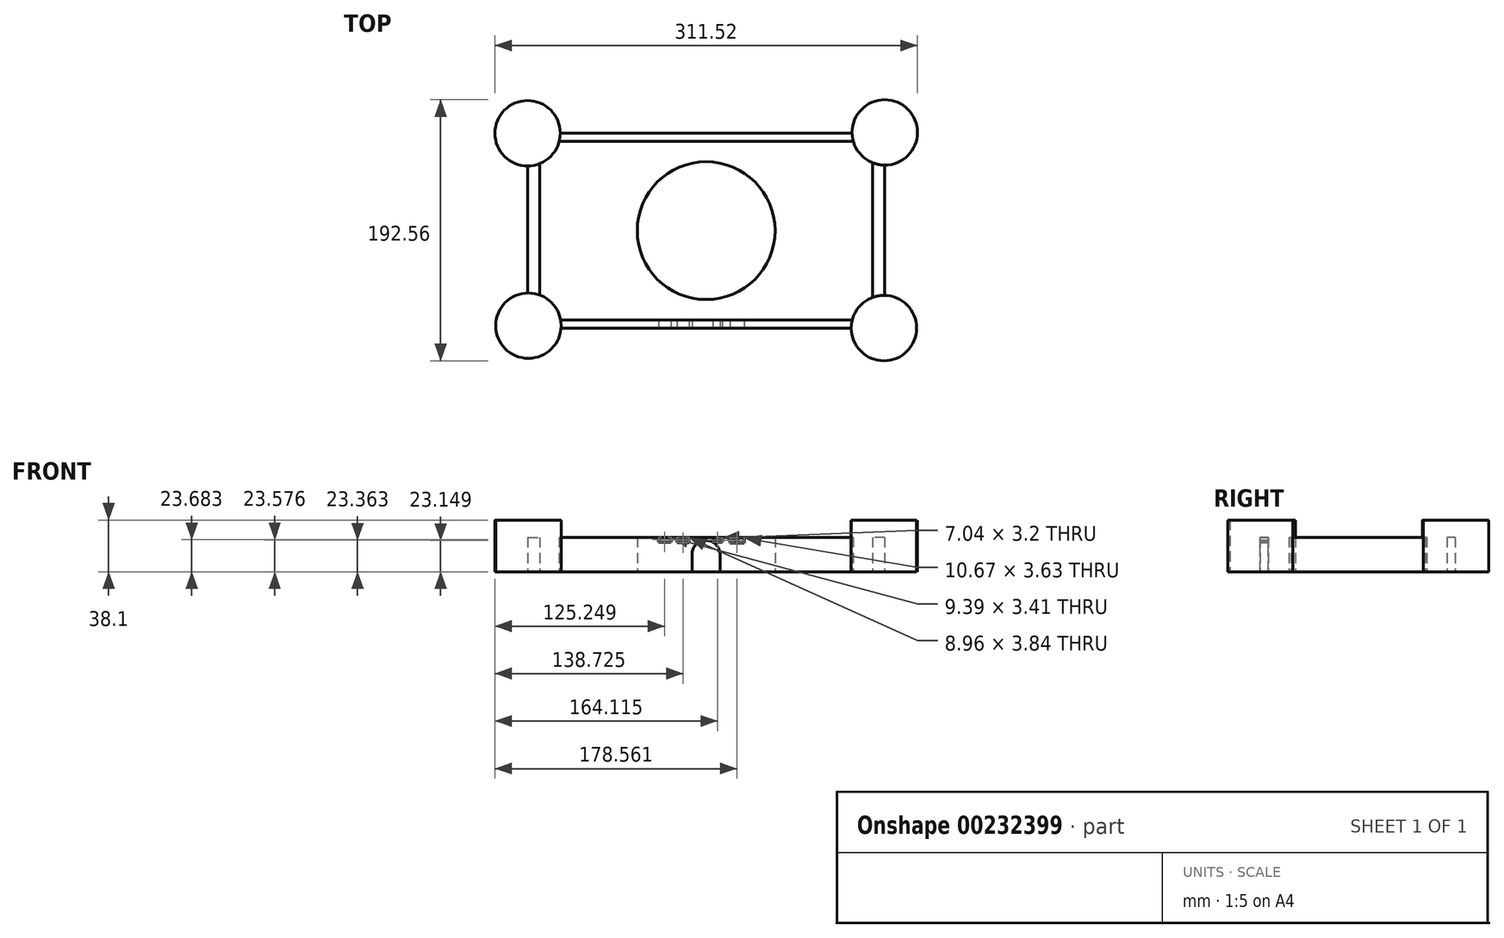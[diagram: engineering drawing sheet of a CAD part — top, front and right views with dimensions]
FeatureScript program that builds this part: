
annotation { "Feature Type Name" : "Feature", "Feature Type Description" : "" }
export const myFeature = defineFeature(function(context is Context, id is Id, definition is map)
    precondition{}
    {
        {
            var Q0;
            Q0=qCreatedBy(makeId("Top.planeOp"),FACE);
            var sketch = newSketch(context, id + "F0", { "sketchPlane" : qUnion([Q0])});
            skLineSegment(sketch, "E0.bottom", {"start": v(131.65, -71.86) * mm, "end": v(131.05, -71.86) * mm});
            skLineSegment(sketch, "E0.top", {"start": v(107.55, 71.86) * mm, "end": v(-107.54, 71.86) * mm});
            skLineSegment(sketch, "E0.left", {"start": v(131.65, -47.76) * mm, "end": v(131.65, 48.36) * mm});
            skLineSegment(sketch, "E0.right", {"start": v(-131.65, -45.95) * mm, "end": v(-131.65, 47.75) * mm});
            skPoint(sketch, "E0.middle", {"position": v(0, 0) * mm});
            skCircle(sketch, "E1", {"center": v(0, 0) * mm, "radius": 50.8 * mm});
            skCircle(sketch, "E2", {"center": v(-131.65, 71.86) * mm, "radius": 24.11 * mm});
            skCircle(sketch, "E3", {"center": v(131.65, 72.47) * mm, "radius": 24.11 * mm});
            skCircle(sketch, "E4", {"center": v(131.05, -71.86) * mm, "radius": 24.11 * mm});
            skCircle(sketch, "E5", {"center": v(-131.07, -70.05) * mm, "radius": 24.11 * mm});
            skLineSegment(sketch, "E6.bottom", {"start": v(108.47, 65.83) * mm, "end": v(-108.3, 65.83) * mm});
            skLineSegment(sketch, "E6.top", {"start": v(107.7, -65.83) * mm, "end": v(-107.33, -65.83) * mm});
            skLineSegment(sketch, "E6.left", {"start": v(122.6, 50.12) * mm, "end": v(122.6, -49.29) * mm});
            skLineSegment(sketch, "E6.right", {"start": v(-122.6, 49.52) * mm, "end": v(-122.6, -47.48) * mm});
            skPoint(sketch, "E7.orphan", {"position": v(131.65, 71.86) * mm});
            skLineSegment(sketch, "E8.trimOffspring", {"start": v(106.94, -71.86) * mm, "end": v(-107.03, -71.86) * mm});
            skPoint(sketch, "E9.orphan", {"position": v(122.6, -65.83) * mm});
            skPoint(sketch, "E10.orphan", {"position": v(-122.6, -65.83) * mm});
            skPoint(sketch, "E11.orphan", {"position": v(-131.65, -71.86) * mm});
            skPoint(sketch, "E12.orphan", {"position": v(-122.6, 65.83) * mm});
            skPoint(sketch, "E13.orphan", {"position": v(122.6, 65.83) * mm});
            skSolve(sketch);
        }
        {
            var Q0;
            {var subQ0=sQuery(id+"F0.wireOp",EDGE,"E0.top");Q0=makeQuery(id+"F0.imprint","IMPRINT",FACE,{"disambiguationData":[TD([[makeQuery(id+"F0.imprint","IMPRINT",EDGE,{"derivedFrom":subQ0}),1.0]])]});}
            var Q1;
            {var subQ0=sQuery(id+"F0.wireOp",EDGE,"E0.right");Q1=makeQuery(id+"F0.imprint","IMPRINT",FACE,{"disambiguationData":[TD([[makeQuery(id+"F0.imprint","IMPRINT",EDGE,{"derivedFrom":subQ0}),-1.0]])]});}
            var Q2;
            {var subQ0=sQuery(id+"F0.wireOp",EDGE,"E6.top");Q2=makeQuery(id+"F0.imprint","IMPRINT",FACE,{"disambiguationData":[TD([[makeQuery(id+"F0.imprint","IMPRINT",EDGE,{"derivedFrom":subQ0}),1.0]])]});}
            var Q3;
            {var subQ0=sQuery(id+"F0.wireOp",EDGE,"E0.left");Q3=makeQuery(id+"F0.imprint","IMPRINT",FACE,{"disambiguationData":[TD([[makeQuery(id+"F0.imprint","IMPRINT",EDGE,{"derivedFrom":subQ0}),1.0]])]});}
            extrude(context, id + "F1", {"entities" : qUnion([Q0, Q1, Q2, Q3]), "depth" : 25.4 * mm});
        }
        {
            var Q0;
            {var subQ0=sQuery(id+"F0.wireOp",EDGE,"E2");var subQ1=makeQuery(id+"F0.imprint","INTERSECT",VERTEX,{"derivedFrom":[sQuery(id+"F0.wireOp",EDGE,"E0.top"),subQ0]});Q0=makeQuery(id+"F0.imprint","IMPRINT",FACE,{"disambiguationData":[TD([[makeQuery(id+"F0.imprint","IMPRINT",EDGE,{"disambiguationData":[TD([[subQ1,-1.0]])],"derivedFrom":subQ0}),1.0]])]});}
            var Q1;
            {var subQ0=sQuery(id+"F0.wireOp",EDGE,"E3");var subQ1=makeQuery(id+"F0.imprint","INTERSECT",VERTEX,{"derivedFrom":[sQuery(id+"F0.wireOp",EDGE,"E0.top"),subQ0]});Q1=makeQuery(id+"F0.imprint","IMPRINT",FACE,{"disambiguationData":[TD([[makeQuery(id+"F0.imprint","IMPRINT",EDGE,{"disambiguationData":[TD([[subQ1,-1.0]])],"derivedFrom":subQ0}),1.0]])]});}
            var Q2;
            {var subQ0=sQuery(id+"F0.wireOp",EDGE,"E5");var subQ1=makeQuery(id+"F0.imprint","INTERSECT",VERTEX,{"derivedFrom":[subQ0,sQuery(id+"F0.wireOp",EDGE,"E6.top")]});Q2=makeQuery(id+"F0.imprint","IMPRINT",FACE,{"disambiguationData":[TD([[makeQuery(id+"F0.imprint","IMPRINT",EDGE,{"disambiguationData":[TD([[subQ1,-1.0]])],"derivedFrom":subQ0}),1.0]])]});}
            var Q3;
            {var subQ0=sQuery(id+"F0.wireOp",EDGE,"E4");var subQ1=makeQuery(id+"F0.imprint","INTERSECT",VERTEX,{"derivedFrom":[sQuery(id+"F0.wireOp",EDGE,"E0.left"),subQ0]});Q3=makeQuery(id+"F0.imprint","IMPRINT",FACE,{"disambiguationData":[TD([[makeQuery(id+"F0.imprint","IMPRINT",EDGE,{"disambiguationData":[TD([[subQ1,-1.0]])],"derivedFrom":subQ0}),1.0]])]});}
            extrude(context, id + "F2", {"entities" : qUnion([Q0, Q1, Q2, Q3]), "depth" : 38.1 * mm});
        }
        {
            var Q0;
            Q0=makeQuery(id+"F1.opExtrude","SWEPT_FACE",FACE,{"disambiguationData":[OSD([sQuery(id+"F0.wireOp",EDGE,"E8.trimOffspring")])]});
            var sketch = newSketch(context, id + "F3", { "sketchPlane" : qUnion([Q0])});
            skLineSegment(sketch, "E14.bottom", {"start": v(-10.48, 0) * mm, "end": v(10.21, 0) * mm});
            skLineSegment(sketch, "E14.left", {"start": v(-10.48, 0) * mm, "end": v(-10.48, 12.8) * mm});
            skLineSegment(sketch, "E14.right", {"start": v(10.21, 0) * mm, "end": v(10.21, 12.8) * mm});
            skArc(sketch, "E15", {"start": v(10.21, 12.8) * mm, "mid": v(-0.14, 23.15) * mm, "end": v(-10.48, 12.8) * mm});
            skLineSegment(sketch, "E16.bottom", {"start": v(-26.67, 20.7) * mm, "end": v(-34.35, 20.7) * mm});
            skLineSegment(sketch, "E16.top", {"start": v(-26.67, 25.39) * mm, "end": v(-34.35, 25.39) * mm});
            skLineSegment(sketch, "E16.left", {"start": v(-26.67, 20.7) * mm, "end": v(-26.67, 25.39) * mm});
            skLineSegment(sketch, "E16.right", {"start": v(-34.35, 20.7) * mm, "end": v(-34.35, 25.39) * mm});
            skPoint(sketch, "E16.middle", {"position": v(-30.51, 23.04) * mm});
            skLineSegment(sketch, "E17.bottom", {"start": v(-15.65, 20.95) * mm, "end": v(-23.65, 20.95) * mm});
            skLineSegment(sketch, "E17.top", {"start": v(-15.65, 25.18) * mm, "end": v(-23.65, 25.18) * mm});
            skLineSegment(sketch, "E17.left", {"start": v(-15.65, 20.95) * mm, "end": v(-15.65, 25.18) * mm});
            skLineSegment(sketch, "E17.right", {"start": v(-23.65, 20.95) * mm, "end": v(-23.65, 25.18) * mm});
            skPoint(sketch, "E17.middle", {"position": v(-19.65, 23.06) * mm});
            skLineSegment(sketch, "E18.bottom", {"start": v(-6.52, 22.23) * mm, "end": v(-12.1, 22.23) * mm});
            skLineSegment(sketch, "E18.top", {"start": v(-6.52, 25.25) * mm, "end": v(-12.1, 25.25) * mm});
            skLineSegment(sketch, "E18.left", {"start": v(-6.52, 22.23) * mm, "end": v(-6.52, 25.25) * mm});
            skLineSegment(sketch, "E18.right", {"start": v(-12.1, 22.23) * mm, "end": v(-12.1, 25.25) * mm});
            skPoint(sketch, "E18.middle", {"position": v(-9.31, 23.74) * mm});
            skLineSegment(sketch, "E19.bottom", {"start": v(3.56, 23.15) * mm, "end": v(-3.65, 23.15) * mm});
            skLineSegment(sketch, "E19.top", {"start": v(3.56, 25.64) * mm, "end": v(-3.65, 25.64) * mm});
            skLineSegment(sketch, "E19.left", {"start": v(3.56, 23.15) * mm, "end": v(3.56, 25.64) * mm});
            skLineSegment(sketch, "E19.right", {"start": v(-3.65, 23.15) * mm, "end": v(-3.65, 25.64) * mm});
            skPoint(sketch, "E19.middle", {"position": v(-0.04, 24.4) * mm});
            skPoint(sketch, "E19.middle.positionSnap0", {"position": v(-0.04, 25.4) * mm});
            skPoint(sketch, "E19.cornerSnap0", {"position": v(-0.14, 23.15) * mm});
            skPoint(sketch, "E19.centerSnap0", {"position": v(-0.04, 25.4) * mm});
            skLineSegment(sketch, "E20.bottom", {"start": v(16.8, 20.98) * mm, "end": v(6.55, 20.98) * mm});
            skLineSegment(sketch, "E20.top", {"start": v(16.8, 25.32) * mm, "end": v(6.55, 25.32) * mm});
            skLineSegment(sketch, "E20.left", {"start": v(16.8, 20.98) * mm, "end": v(16.8, 25.32) * mm});
            skLineSegment(sketch, "E20.right", {"start": v(6.55, 20.98) * mm, "end": v(6.55, 25.32) * mm});
            skPoint(sketch, "E20.middle", {"position": v(11.67, 23.15) * mm});
            skLineSegment(sketch, "E21.bottom", {"start": v(30.23, 21.3) * mm, "end": v(19.56, 21.3) * mm});
            skLineSegment(sketch, "E21.top", {"start": v(30.23, 25) * mm, "end": v(19.56, 25) * mm});
            skLineSegment(sketch, "E21.left", {"start": v(30.23, 21.3) * mm, "end": v(30.23, 25) * mm});
            skLineSegment(sketch, "E21.right", {"start": v(19.56, 21.3) * mm, "end": v(19.56, 25) * mm});
            skPoint(sketch, "E21.middle", {"position": v(24.9, 23.15) * mm});
            skSolve(sketch);
        }
        {
            var Q0;
            Q0=makeQuery(id+"F3.imprint","IMPRINT",FACE,{"disambiguationData":[TD([[makeQuery(id+"F3.imprint","IMPRINT",EDGE,{"derivedFrom":sQuery(id+"F3.wireOp",EDGE,"E14.bottom")}),-1.0]])]});
            extrude(context, id + "F4", {"entities" : qUnion([Q0]), "operationType" : NewBodyOperationType.REMOVE, "oppositeDirection" : true, "depth" : 25.4 * mm});
        }
        {
            var Q0;
            Q0=makeQuery(id+"F1.opExtrude","SWEPT_FACE",FACE,{"disambiguationData":[OSD([sQuery(id+"F0.wireOp",EDGE,"E8.trimOffspring")])]});
            var sketch = newSketch(context, id + "F5", { "sketchPlane" : qUnion([Q0])});
            skLineSegment(sketch, "E22.bottom", {"start": v(-25.82, 21.98) * mm, "end": v(-35.2, 21.98) * mm});
            skLineSegment(sketch, "E22.top", {"start": v(-25.82, 25.39) * mm, "end": v(-35.2, 25.39) * mm});
            skLineSegment(sketch, "E22.left", {"start": v(-25.82, 21.98) * mm, "end": v(-25.82, 25.39) * mm});
            skLineSegment(sketch, "E22.right", {"start": v(-35.2, 21.98) * mm, "end": v(-35.2, 25.39) * mm});
            skPoint(sketch, "E22.middle", {"position": v(-30.51, 23.68) * mm});
            skLineSegment(sketch, "E23.bottom", {"start": v(28.13, 21.34) * mm, "end": v(17.47, 21.34) * mm});
            skLineSegment(sketch, "E23.top", {"start": v(28.13, 24.96) * mm, "end": v(17.47, 24.96) * mm});
            skLineSegment(sketch, "E23.left", {"start": v(28.13, 21.34) * mm, "end": v(28.13, 24.96) * mm});
            skLineSegment(sketch, "E23.right", {"start": v(17.47, 21.34) * mm, "end": v(17.47, 24.96) * mm});
            skPoint(sketch, "E23.middle", {"position": v(22.8, 23.15) * mm});
            skPoint(sketch, "E23.middle.positionSnap0", {"position": v(-0.14, 23.15) * mm});
            skPoint(sketch, "E23.centerSnap0", {"position": v(-0.14, 23.15) * mm});
            skSolve(sketch);
        }
        {
            var Q0;
            Q0=makeQuery(id+"F5.imprint","IMPRINT",FACE,{"disambiguationData":[TD([[makeQuery(id+"F5.imprint","IMPRINT",EDGE,{"derivedFrom":sQuery(id+"F5.wireOp",EDGE,"E22.bottom")}),-1.0]])]});
            var Q1;
            Q1=makeQuery(id+"F5.imprint","IMPRINT",FACE,{"disambiguationData":[TD([[makeQuery(id+"F5.imprint","IMPRINT",EDGE,{"derivedFrom":sQuery(id+"F5.wireOp",EDGE,"E23.bottom")}),-1.0]])]});
            extrude(context, id + "F6", {"entities" : qUnion([Q0, Q1]), "operationType" : NewBodyOperationType.REMOVE, "oppositeDirection" : true, "depth" : 25.4 * mm});
        }
        {
            var Q0;
            Q0=makeQuery(id+"F1.opExtrude","SWEPT_FACE",FACE,{"disambiguationData":[OSD([sQuery(id+"F0.wireOp",EDGE,"E8.trimOffspring")])]});
            var sketch = newSketch(context, id + "F7", { "sketchPlane" : qUnion([Q0])});
            skLineSegment(sketch, "E24.bottom", {"start": v(-12.55, 21.44) * mm, "end": v(-21.52, 21.44) * mm});
            skLineSegment(sketch, "E24.top", {"start": v(-12.55, 25.28) * mm, "end": v(-21.52, 25.28) * mm});
            skLineSegment(sketch, "E24.left", {"start": v(-12.55, 21.44) * mm, "end": v(-12.55, 25.28) * mm});
            skLineSegment(sketch, "E24.right", {"start": v(-21.52, 21.44) * mm, "end": v(-21.52, 25.28) * mm});
            skPoint(sketch, "E24.middle", {"position": v(-17.03, 23.36) * mm});
            skLineSegment(sketch, "E25.bottom", {"start": v(11.88, 21.98) * mm, "end": v(4.83, 21.98) * mm});
            skLineSegment(sketch, "E25.top", {"start": v(11.88, 25.18) * mm, "end": v(4.83, 25.18) * mm});
            skLineSegment(sketch, "E25.left", {"start": v(11.88, 21.98) * mm, "end": v(11.88, 25.18) * mm});
            skLineSegment(sketch, "E25.right", {"start": v(4.83, 21.98) * mm, "end": v(4.83, 25.18) * mm});
            skPoint(sketch, "E25.middle", {"position": v(8.35, 23.58) * mm});
            skSolve(sketch);
        }
        {
            var Q0;
            Q0 = qSketchRegion(id + "F7", true);
            extrude(context, id + "F8", {"entities" : qUnion([Q0]), "operationType" : NewBodyOperationType.REMOVE, "oppositeDirection" : true, "depth" : 25.4 * mm});
        }
        {
            var Q0;
            Q0=makeQuery(id+"F0.imprint","IMPRINT",FACE,{"disambiguationData":[TD([[makeQuery(id+"F0.imprint","IMPRINT",EDGE,{"derivedFrom":sQuery(id+"F0.wireOp",EDGE,"E1")}),1.0]])]});
            extrude(context, id + "F9", {"entities" : qUnion([Q0]), "depth" : 25.4 * mm});
        }
    });
